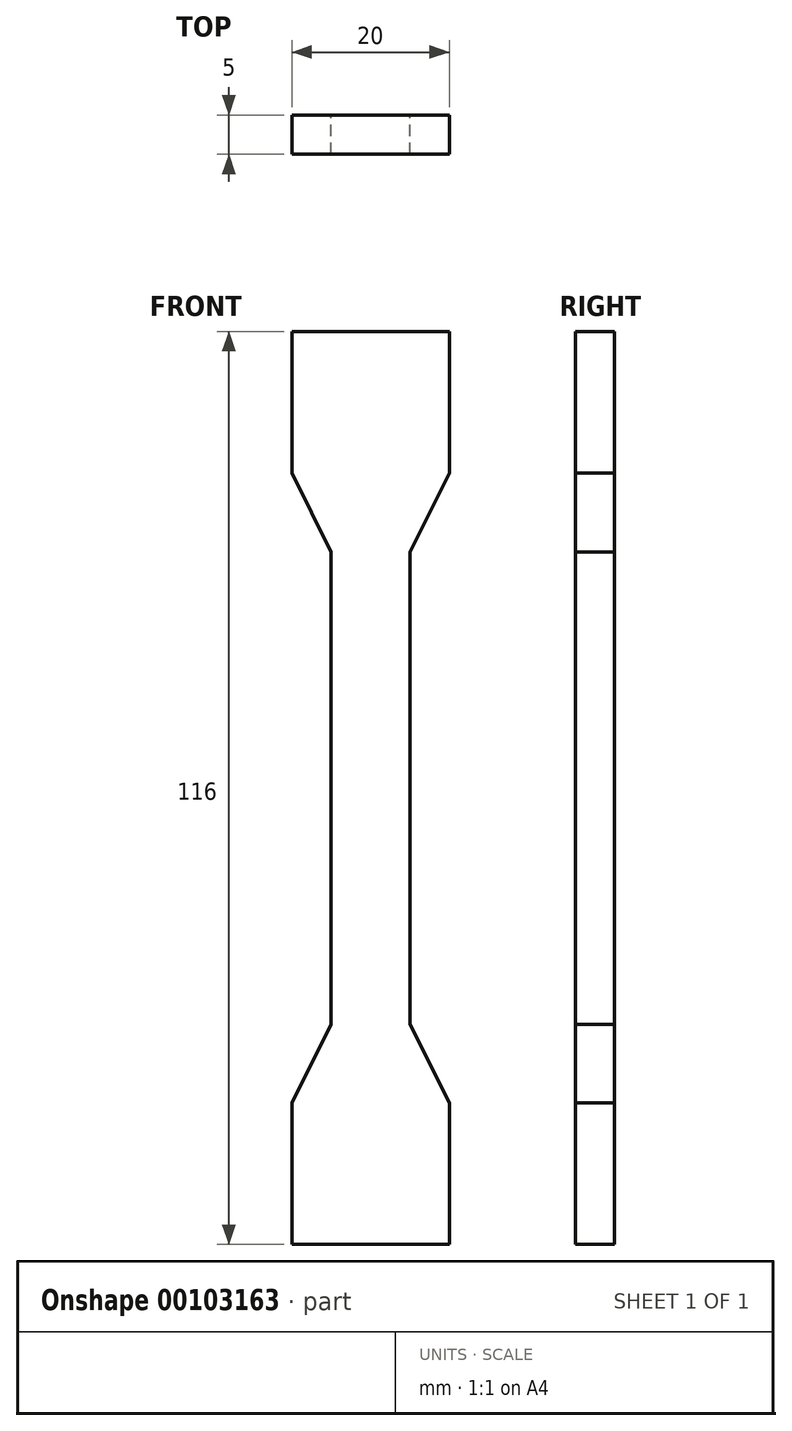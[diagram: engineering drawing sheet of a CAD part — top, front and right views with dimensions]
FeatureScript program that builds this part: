
annotation { "Feature Type Name" : "Feature", "Feature Type Description" : "" }
export const myFeature = defineFeature(function(context is Context, id is Id, definition is map)
    precondition{}
    {
        {
            var Q0;
            Q0=qCreatedBy(makeId("Front.planeOp"),FACE);
            var sketch = newSketch(context, id + "F0", { "sketchPlane" : qUnion([Q0])});
            skLineSegment(sketch, "E0", {"start": v(0, 0) * mm, "end": v(0, 58) * mm, "construction": true});
            skLineSegment(sketch, "E1", {"start": v(0, 58) * mm, "end": v(-10, 58) * mm});
            skLineSegment(sketch, "E2", {"start": v(-10, 58) * mm, "end": v(-10, 40) * mm});
            skLineSegment(sketch, "E3", {"start": v(-10, 40) * mm, "end": v(-5, 30) * mm});
            skLineSegment(sketch, "E4", {"start": v(-5, 30) * mm, "end": v(-5, 0) * mm});
            skLineSegment(sketch, "E5", {"start": v(-5, 0) * mm, "end": v(0, 0) * mm, "construction": true});
            skLineSegment(sketch, "E6.MirrorCS", {"start": v(10, 58) * mm, "end": v(10, 40) * mm});
            skLineSegment(sketch, "E7.MirrorCS", {"start": v(10, 40) * mm, "end": v(5, 30) * mm});
            skLineSegment(sketch, "E8.MirrorCS", {"start": v(5, 30) * mm, "end": v(5, 0) * mm});
            skLineSegment(sketch, "E9.MirrorCS", {"start": v(0, 58) * mm, "end": v(10, 58) * mm});
            skLineSegment(sketch, "E10.MirrorCS", {"start": v(0, -58) * mm, "end": v(10, -58) * mm});
            skLineSegment(sketch, "E11.MirrorCS", {"start": v(5, -30) * mm, "end": v(5, 0) * mm});
            skLineSegment(sketch, "E12.MirrorCS", {"start": v(10, -40) * mm, "end": v(5, -30) * mm});
            skLineSegment(sketch, "E13.MirrorCS", {"start": v(0, 0) * mm, "end": v(0, -58) * mm, "construction": true});
            skLineSegment(sketch, "E14.MirrorCS", {"start": v(0, -58) * mm, "end": v(-10, -58) * mm});
            skLineSegment(sketch, "E15.MirrorCS", {"start": v(10, -58) * mm, "end": v(10, -40) * mm});
            skLineSegment(sketch, "E16.MirrorCS", {"start": v(-10, -58) * mm, "end": v(-10, -40) * mm});
            skLineSegment(sketch, "E17.MirrorCS", {"start": v(-10, -40) * mm, "end": v(-5, -30) * mm});
            skLineSegment(sketch, "E18.MirrorCS", {"start": v(-5, -30) * mm, "end": v(-5, 0) * mm});
            skSolve(sketch);
        }
        {
            var Q0;
            Q0 = qSketchRegion(id + "F0", true);
            extrude(context, id + "F1", {"entities" : qUnion([Q0]), "endBound" : BoundingType.SYMMETRIC, "depth" : 5 * mm});
        }
    });
